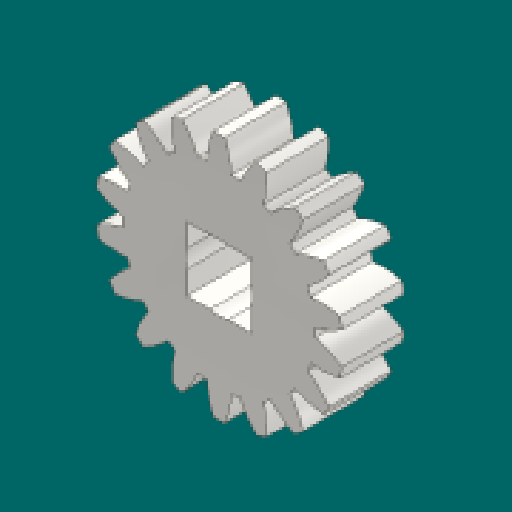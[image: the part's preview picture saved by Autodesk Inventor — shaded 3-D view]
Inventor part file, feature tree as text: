
AUTODESK INVENTOR PART (.ipt)
format: ipt  version: 2023.1 (Build 271208000, 208)  size: 330,752 bytes
history: native  units: mm (DEFAULTED — no unit token found)
features: sketch x4, extrude x3, plane x3, other x3, chamfer x1, projected_geometry x1
ambient origin geometry x8: Origin, YZ Plane, XZ Plane, XY Plane, X Axis, Y Axis, Z Axis, Center Point
bodies: Solid1 (feature_tree)
feature tree (15):
  extrude  "Extrusion1"  Depth=6.35mm TaperAngle=0.0deg
  plane  "Work Plane1"
  plane  "Work Plane2"
  plane  "Work Plane3"
  other  "Spur Gear"
  extrude  "Extrusion2"  Depth=76.2mm TaperAngle=0.0deg
  extrude  "Extrusion3"  TaperAngle=0.0deg  [1 undecoded]
  chamfer  "Chamfer1"  Distance=22.86mm
  sketch  "Sketch1"  dims[d0=25.4mm d1=6.35mm d2=0.0mm]
  sketch  "Sketch2"  dims[d3=22.86mm d4=76.2mm d5=0.0mm]
  other  "Srf1"
  sketch  "Sketch3"  dims[d6=0.0mm d7=1.745329mm d9=0.0mm d14=0.0mm d15=22.86mm]
  sketch  "Sketch4"  dims[d16=0.0mm d17=0.0mm d18=0.0mm d19=22.86mm d20=6.604mm d21=6.604mm d22=6.858mm d23=0.0mm d24=0.0mm d25=12.7mm d26=1.2mm d27=0.0mm d28=0.6mm d29=3.175mm d30=45.0deg]
  projected_geometry  "Projected Loop1"
  other  "Pitch Diameter"
note: 1 required parameter value undecoded (feature->parameter linkage not recoverable at this tier; creation-order binding heuristic only, values carry confidence <= 0.55)
